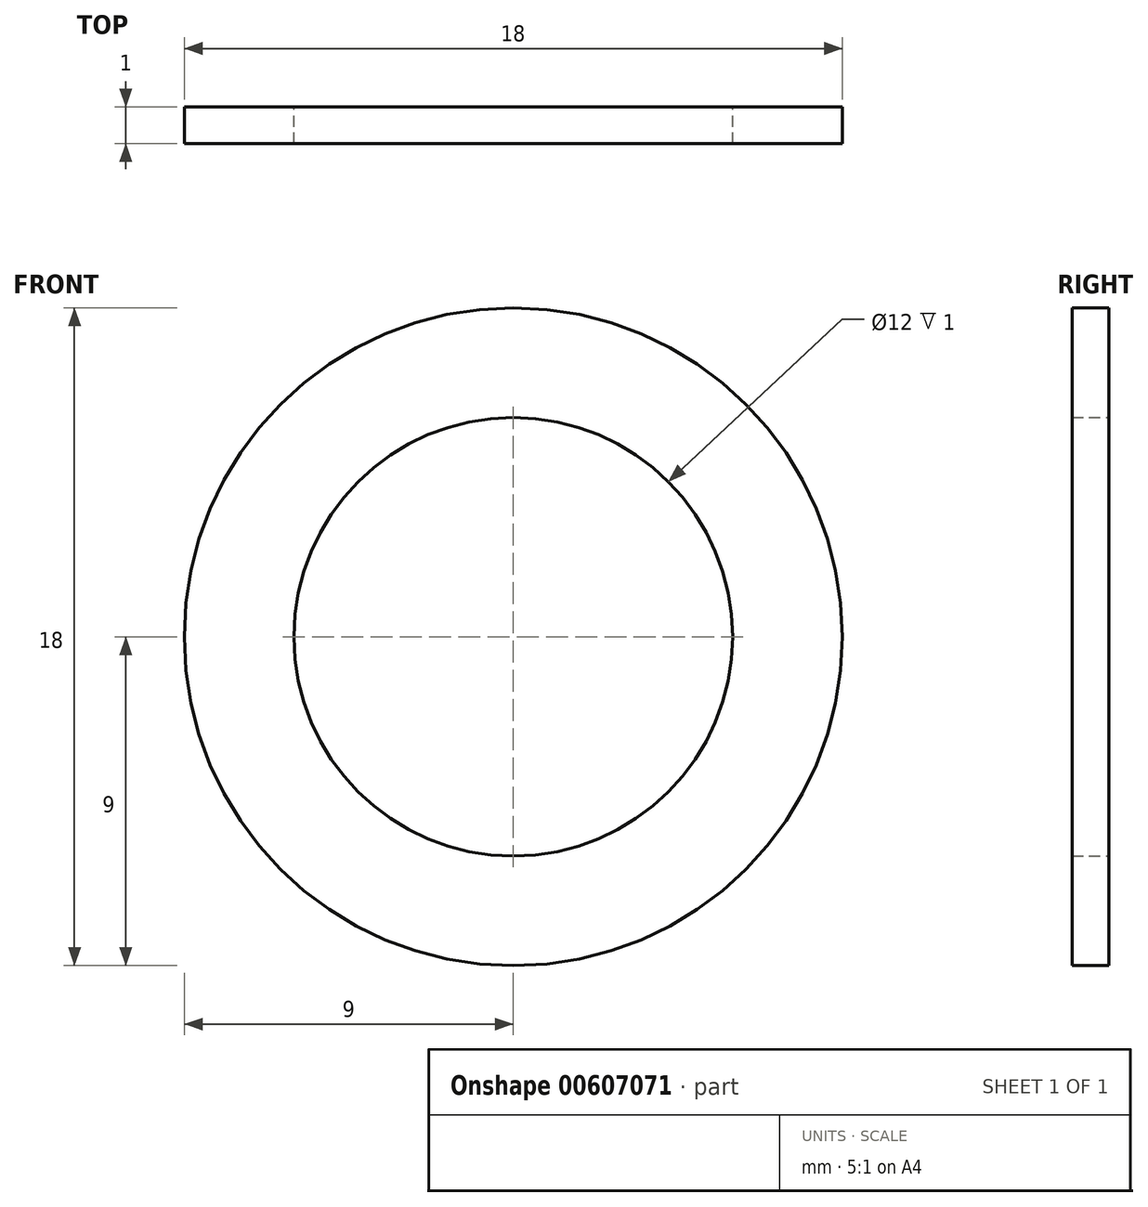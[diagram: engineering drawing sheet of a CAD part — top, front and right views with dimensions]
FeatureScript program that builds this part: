
annotation { "Feature Type Name" : "Feature", "Feature Type Description" : "" }
export const myFeature = defineFeature(function(context is Context, id is Id, definition is map)
    precondition{}
    {
        {
            var Q0;
            Q0=qCreatedBy(makeId("Front.planeOp"),FACE);
            var sketch = newSketch(context, id + "F0", { "sketchPlane" : qUnion([Q0]) });
            skCircle(sketch, "E0", {"center": v(0, 0) * mm, "radius": 9 * mm});
            skCircle(sketch, "E1", {"center": v(0, 0) * mm, "radius": 6 * mm});
            skSolve(sketch);
        }
        {
            var Q0;
            Q0=makeQuery(id+"F0.imprint","IMPRINT",FACE,{"disambiguationData":[TD([[makeQuery(id+"F0.imprint","IMPRINT",EDGE,{"derivedFrom":sQuery(id+"F0.wireOp",EDGE,"E0")}),1.0]])]});
            extrude(context, id + "F1", {"entities" : qUnion([Q0]), "depth" : 1 * mm, "offsetDistance" : 25 * mm});
        }
    });
